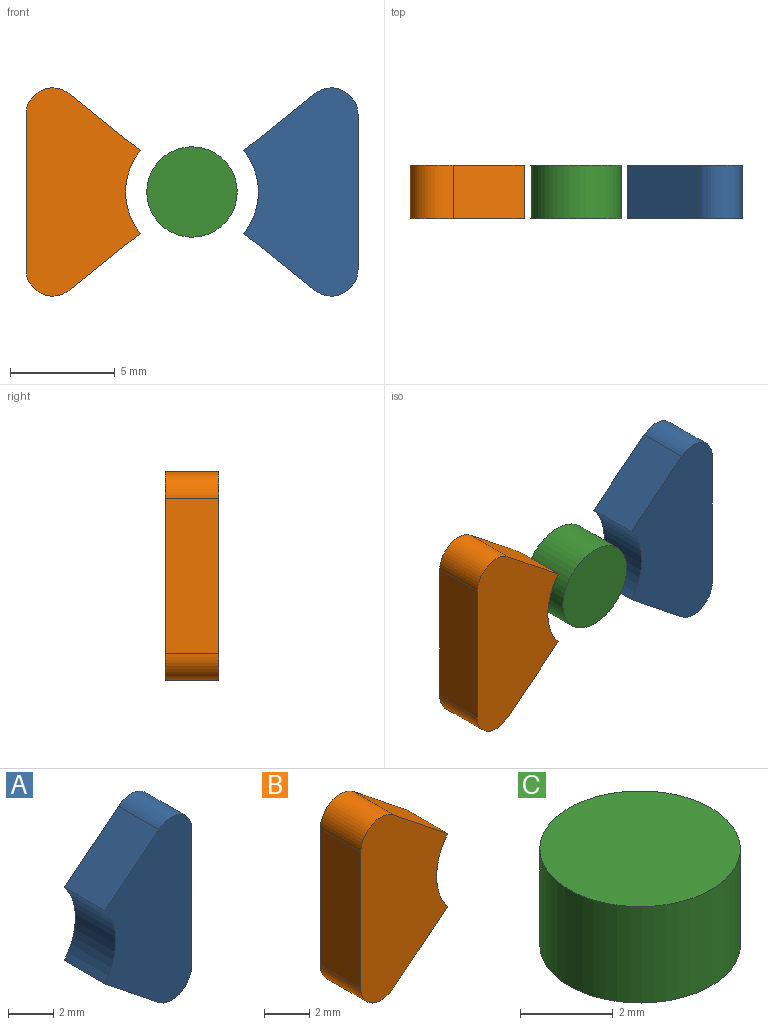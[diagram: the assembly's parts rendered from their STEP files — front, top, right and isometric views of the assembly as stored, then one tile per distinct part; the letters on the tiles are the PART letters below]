
ASSEMBLY  parts=3 mates=2
PART A: 8 faces, bbox 5.5x2.5x10 mm
  f0: plane 3.4x2.72mm, normal (-0.62,0,0.78), area 11mm2, adj f1,f4,f5,f6
  f1: cylinder r=3.17mm len=3.97mm, axis (0,1,0), area 10.9mm2, adj f0,f2,f4,f5
  f2: plane 3.4x2.72mm, normal (-0.62,0,-0.78), area 11mm2, adj f1,f4,f5,f7
  f3: plane 7.42x2.54mm, normal (1,0,0), area 18.8mm2, adj f4,f5,f6,f7
  f4: plane 9.96x5.46mm, normal (0,-1,0), area 40.5mm2, adj f0,f1,f2,f3,f6,f7
  f5: plane 9.96x5.46mm, normal (0,1,0), area 40.5mm2, adj f0,f1,f2,f3,f6,f7
  f6: cylinder r=1.27mm len=2.54mm, axis (0,1,0), area 7.2mm2, adj f0,f3,f4,f5
  f7: cylinder r=1.27mm len=2.54mm, axis (0,1,0), area 7.2mm2, adj f2,f3,f4,f5
PART B: 8 faces, bbox 5.5x2.5x10 mm
  f0: cylinder r=3.17mm len=3.97mm, axis (0,1,0), area 10.9mm2, adj f1,f3,f4,f5
  f1: plane 3.4x2.72mm, normal (0.62,0,0.78), area 11mm2, adj f0,f4,f5,f6
  f2: plane 7.42x2.54mm, normal (-1,0,0), area 18.8mm2, adj f4,f5,f6,f7
  f3: plane 3.4x2.72mm, normal (0.62,0,-0.78), area 11mm2, adj f0,f4,f5,f7
  f4: plane 9.96x5.46mm, normal (0,-1,0), area 40.5mm2, adj f0,f1,f2,f3,f6,f7
  f5: plane 9.96x5.46mm, normal (0,1,0), area 40.5mm2, adj f0,f1,f2,f3,f6,f7
  f6: cylinder r=1.27mm len=2.54mm, axis (0,1,0), area 7.2mm2, adj f1,f2,f4,f5
  f7: cylinder r=1.27mm len=2.54mm, axis (0,1,0), area 7.2mm2, adj f2,f3,f4,f5
PART C: 3 faces, bbox 4.3x4.3x2.5 mm
  f0: cylinder r=2.16mm len=4.32mm, axis (0,0,-1), area 34.5mm2, adj f1,f2
  f1: plane 4.32x4.32mm, normal (0,0,1), area 14.6mm2, adj f0
  f2: plane 4.32x4.32mm, normal (0,0,-1), area 14.6mm2, adj f0
PLACE A t=(9.42,-19.98,-11.54)mm
PLACE B t=(9.42,-19.98,-11.54)mm
PLACE C rot(axis=(1,0,0),90deg) t=(-26.1,-19.98,-8.58)mm
MATE fastened A.f1 <-> C.f0  axis (0,1,0) through (-35.26,-21.25,4.91)mm
MATE fastened C.f0 <-> B.f0  axis (0,1,0) through (-35.26,-21.25,4.91)mm
